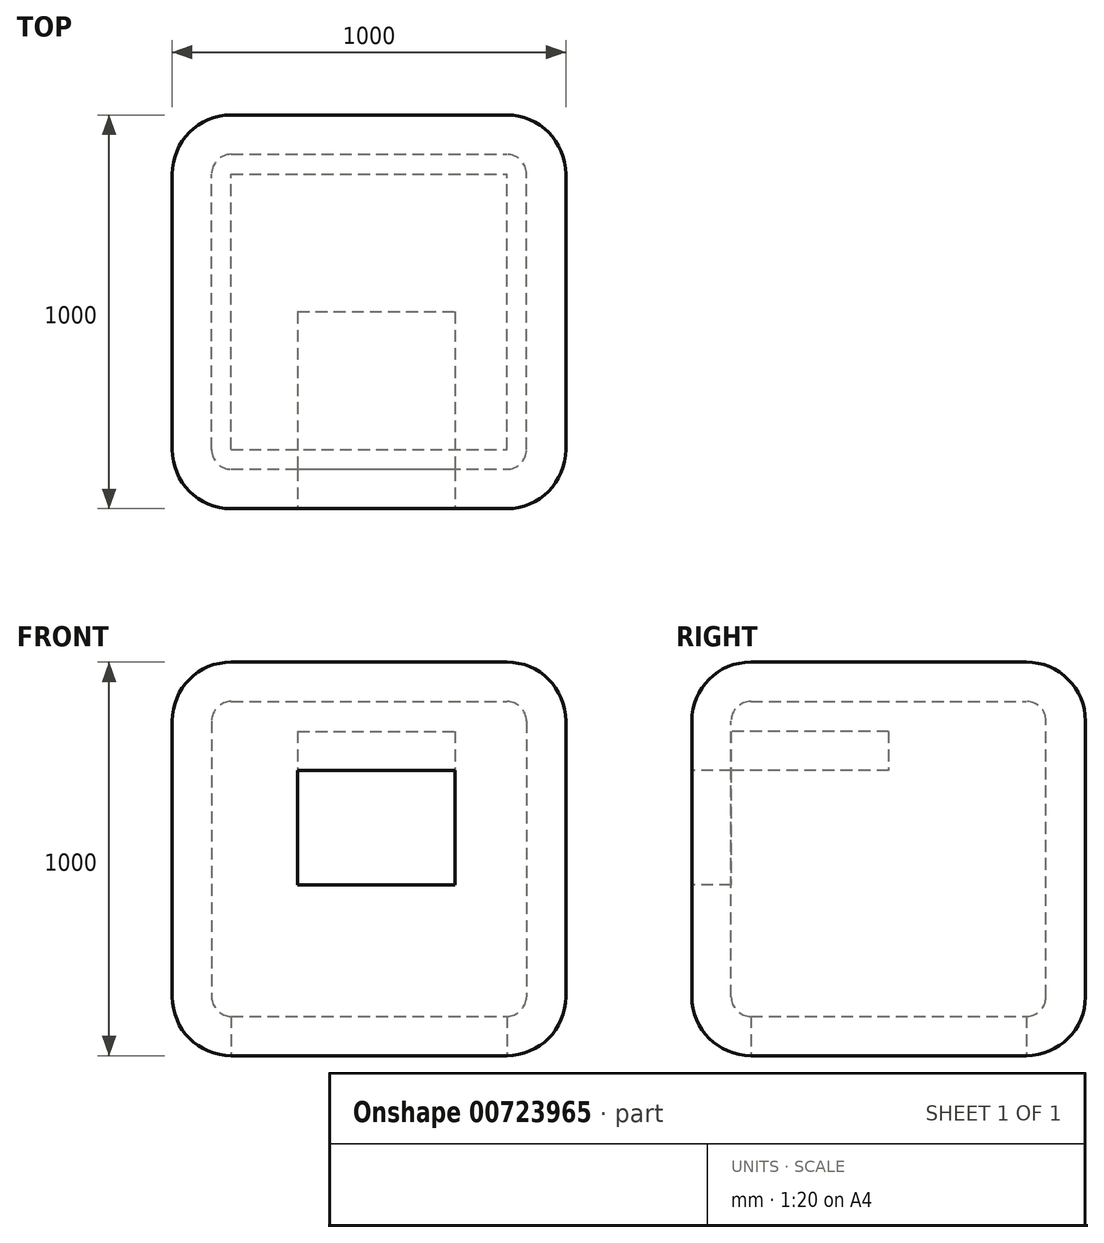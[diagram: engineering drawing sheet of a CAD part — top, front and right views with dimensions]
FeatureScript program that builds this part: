
annotation { "Feature Type Name" : "Feature", "Feature Type Description" : "" }
export const myFeature = defineFeature(function(context is Context, id is Id, definition is map)
    precondition{}
    {
        {
            var Q0;
            Q0=qCreatedBy(makeId("Front.planeOp"),FACE);
            var sketch = newSketch(context, id + "F0", { "sketchPlane" : qUnion([Q0])});
            skLineSegment(sketch, "E0.bottom", {"start": v(-318.37, 840.37) * mm, "end": v(681.63, 840.37) * mm});
            skLineSegment(sketch, "E0.top", {"start": v(-318.37, -159.63) * mm, "end": v(681.63, -159.63) * mm});
            skLineSegment(sketch, "E0.left", {"start": v(-318.37, 840.37) * mm, "end": v(-318.37, -159.63) * mm});
            skLineSegment(sketch, "E0.right", {"start": v(681.63, 840.37) * mm, "end": v(681.63, -159.63) * mm});
            skSolve(sketch);
        }
        {
            var Q0;
            Q0 = qSketchRegion(id + "F0", true);
            extrude(context, id + "F1", {"entities" : qUnion([Q0]), "depth" : 1000 * mm, "offsetDistance" : 25 * mm});
        }
        {
            var Q0;
            Q0=makeQuery(id+"F1.opExtrude","CAP_EDGE",EDGE,{"disambiguationData":[OSD([sQuery(id+"F0.wireOp",EDGE,"E0.bottom")])],"isStart":false});
            var Q1;
            Q1=makeQuery(id+"F1.opExtrude","SWEPT_EDGE",EDGE,{"disambiguationData":[OSD([sQuery(id+"F0.wireOp",EDGE,"E0.bottom"),sQuery(id+"F0.wireOp",EDGE,"E0.right")])]});
            var Q2;
            Q2=makeQuery(id+"F1.opExtrude","CAP_EDGE",EDGE,{"disambiguationData":[OSD([sQuery(id+"F0.wireOp",EDGE,"E0.right")])],"isStart":false});
            var Q3;
            Q3=makeQuery(id+"F1.opExtrude","CAP_EDGE",EDGE,{"disambiguationData":[OSD([sQuery(id+"F0.wireOp",EDGE,"E0.left")])],"isStart":false});
            var Q4;
            Q4=makeQuery(id+"F1.opExtrude","SWEPT_EDGE",EDGE,{"disambiguationData":[OSD([sQuery(id+"F0.wireOp",EDGE,"E0.bottom"),sQuery(id+"F0.wireOp",EDGE,"E0.left")])]});
            var Q5;
            Q5=makeQuery(id+"F1.opExtrude","CAP_EDGE",EDGE,{"disambiguationData":[OSD([sQuery(id+"F0.wireOp",EDGE,"E0.bottom")])],"isStart":true});
            var Q6;
            Q6=makeQuery(id+"F1.opExtrude","CAP_EDGE",EDGE,{"disambiguationData":[OSD([sQuery(id+"F0.wireOp",EDGE,"E0.right")])],"isStart":true});
            var Q7;
            Q7=makeQuery(id+"F1.opExtrude","CAP_EDGE",EDGE,{"disambiguationData":[OSD([sQuery(id+"F0.wireOp",EDGE,"E0.left")])],"isStart":true});
            var Q8;
            Q8=makeQuery(id+"F1.opExtrude","CAP_EDGE",EDGE,{"disambiguationData":[OSD([sQuery(id+"F0.wireOp",EDGE,"E0.top")])],"isStart":false});
            var Q9;
            Q9=makeQuery(id+"F1.opExtrude","SWEPT_EDGE",EDGE,{"disambiguationData":[OSD([sQuery(id+"F0.wireOp",EDGE,"E0.top"),sQuery(id+"F0.wireOp",EDGE,"E0.right")])]});
            var Q10;
            Q10=makeQuery(id+"F1.opExtrude","SWEPT_EDGE",EDGE,{"disambiguationData":[OSD([sQuery(id+"F0.wireOp",EDGE,"E0.top"),sQuery(id+"F0.wireOp",EDGE,"E0.left")])]});
            var Q11;
            Q11=makeQuery(id+"F1.opExtrude","CAP_EDGE",EDGE,{"disambiguationData":[OSD([sQuery(id+"F0.wireOp",EDGE,"E0.top")])],"isStart":true});
            fillet(context, id + "F2", {"entities" : qUnion([Q0, Q1, Q2, Q3, Q4, Q5, Q6, Q7, Q8, Q9, Q10, Q11]), "radius" : 150 * mm, "tangentPropagation" : true, "allowEdgeOverflow" : false});
        }
        {
            var Q0;
            Q0=makeQuery(id+"F1.opExtrude","CAP_FACE",FACE,{"disambiguationData":[OSD([sQuery(id+"F0.wireOp",EDGE,"E0.bottom"),sQuery(id+"F0.wireOp",EDGE,"E0.top"),sQuery(id+"F0.wireOp",EDGE,"E0.left"),sQuery(id+"F0.wireOp",EDGE,"E0.right")])],"isStart":false});
            var sketch = newSketch(context, id + "F3", { "sketchPlane" : qUnion([Q0])});
            skLineSegment(sketch, "E1.bottom", {"start": v(0, 564.52) * mm, "end": v(400, 564.52) * mm});
            skLineSegment(sketch, "E1.top", {"start": v(0, 274.52) * mm, "end": v(400, 274.52) * mm});
            skLineSegment(sketch, "E1.left", {"start": v(0, 564.52) * mm, "end": v(0, 274.52) * mm});
            skLineSegment(sketch, "E1.right", {"start": v(400, 564.52) * mm, "end": v(400, 274.52) * mm});
            skSolve(sketch);
        }
        {
            var Q0;
            Q0 = qSketchRegion(id + "F3", true);
            extrude(context, id + "F4", {"entities" : qUnion([Q0]), "operationType" : NewBodyOperationType.REMOVE, "oppositeDirection" : true, "depth" : 500 * mm, "offsetDistance" : 25 * mm});
        }
        {
            var Q0;
            Q0=makeQuery(id+"F4.boolean.opBoolean","COPY",FACE,{"derivedFrom":makeQuery(id+"F4.opExtrude","SWEPT_FACE",FACE,{"disambiguationData":[OSD([sQuery(id+"F3.wireOp",EDGE,"E1.top")])]})});
            var Q1;
            Q1=makeQuery(id+"F4.boolean.opBoolean","COPY",FACE,{"derivedFrom":makeQuery(id+"F4.opExtrude","SWEPT_FACE",FACE,{"disambiguationData":[OSD([sQuery(id+"F3.wireOp",EDGE,"E1.left")])]})});
            var Q2;
            Q2=makeQuery(id+"F4.boolean.opBoolean","COPY",FACE,{"derivedFrom":makeQuery(id+"F4.opExtrude","SWEPT_FACE",FACE,{"disambiguationData":[OSD([sQuery(id+"F3.wireOp",EDGE,"E1.right")])]})});
            var Q3;
            Q3=makeQuery(id+"F4.boolean.opBoolean","COPY",FACE,{"derivedFrom":makeQuery(id+"F4.opExtrude","CAP_FACE",FACE,{"disambiguationData":[OSD([sQuery(id+"F3.wireOp",EDGE,"E1.bottom"),sQuery(id+"F3.wireOp",EDGE,"E1.top"),sQuery(id+"F3.wireOp",EDGE,"E1.left"),sQuery(id+"F3.wireOp",EDGE,"E1.right")])],"isStart":false})});
            shell(context, id + "F5", {"entities" : qUnion([Q0, Q1, Q2, Q3]), "thickness" : 100 * mm});
        }
        {
            var Q0;
            Q0=makeQuery(id+"F1.opExtrude","SWEPT_FACE",FACE,{"disambiguationData":[OSD([sQuery(id+"F0.wireOp",EDGE,"E0.top")])]});
            var sketch = newSketch(context, id + "F6", { "sketchPlane" : qUnion([Q0])});
            skLineSegment(sketch, "E2.bottom", {"start": v(-168.37, 850) * mm, "end": v(531.63, 850) * mm});
            skLineSegment(sketch, "E2.top", {"start": v(-168.37, 150) * mm, "end": v(531.63, 150) * mm});
            skLineSegment(sketch, "E2.left", {"start": v(-168.37, 850) * mm, "end": v(-168.37, 150) * mm});
            skLineSegment(sketch, "E2.right", {"start": v(531.63, 850) * mm, "end": v(531.63, 150) * mm});
            skSolve(sketch);
        }
        {
            var Q0;
            Q0 = qSketchRegion(id + "F6", true);
            extrude(context, id + "F7", {"entities" : qUnion([Q0]), "operationType" : NewBodyOperationType.REMOVE, "oppositeDirection" : true, "depth" : 500 * mm, "offsetDistance" : 25 * mm});
        }
    });
